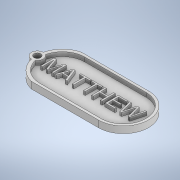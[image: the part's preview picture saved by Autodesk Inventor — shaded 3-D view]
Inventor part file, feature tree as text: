
AUTODESK INVENTOR PART (.ipt)
format: ipt  version: 2020 (Build 240168000, 168)  size: 229,376 bytes
history: native  units: mm
features: sketch x2, extrude x2, emboss x1
ambient origin geometry x8: Origin, YZ Plane, XZ Plane, XY Plane, X Axis, Y Axis, Z Axis, Center Point
bodies: Solid1 (feature_tree)
feature tree (5):
  sketch  "Sketch1"  dims[d2=30.0mm d8=7.0mm]
  extrude  "Extrusion1"  Depth=7.0mm
  extrude  "Extrusion2"  Depth=1.5mm TaperAngle=0.0deg
  emboss  "Emboss1"
  sketch  "Sketch2"  dims[d9=4.0mm d13=1.5mm d14=0.0mm d15=4.0mm d16=0.0mm d20=2.0mm d21=0.0mm d28=27.0mm d29=70.0mm]
